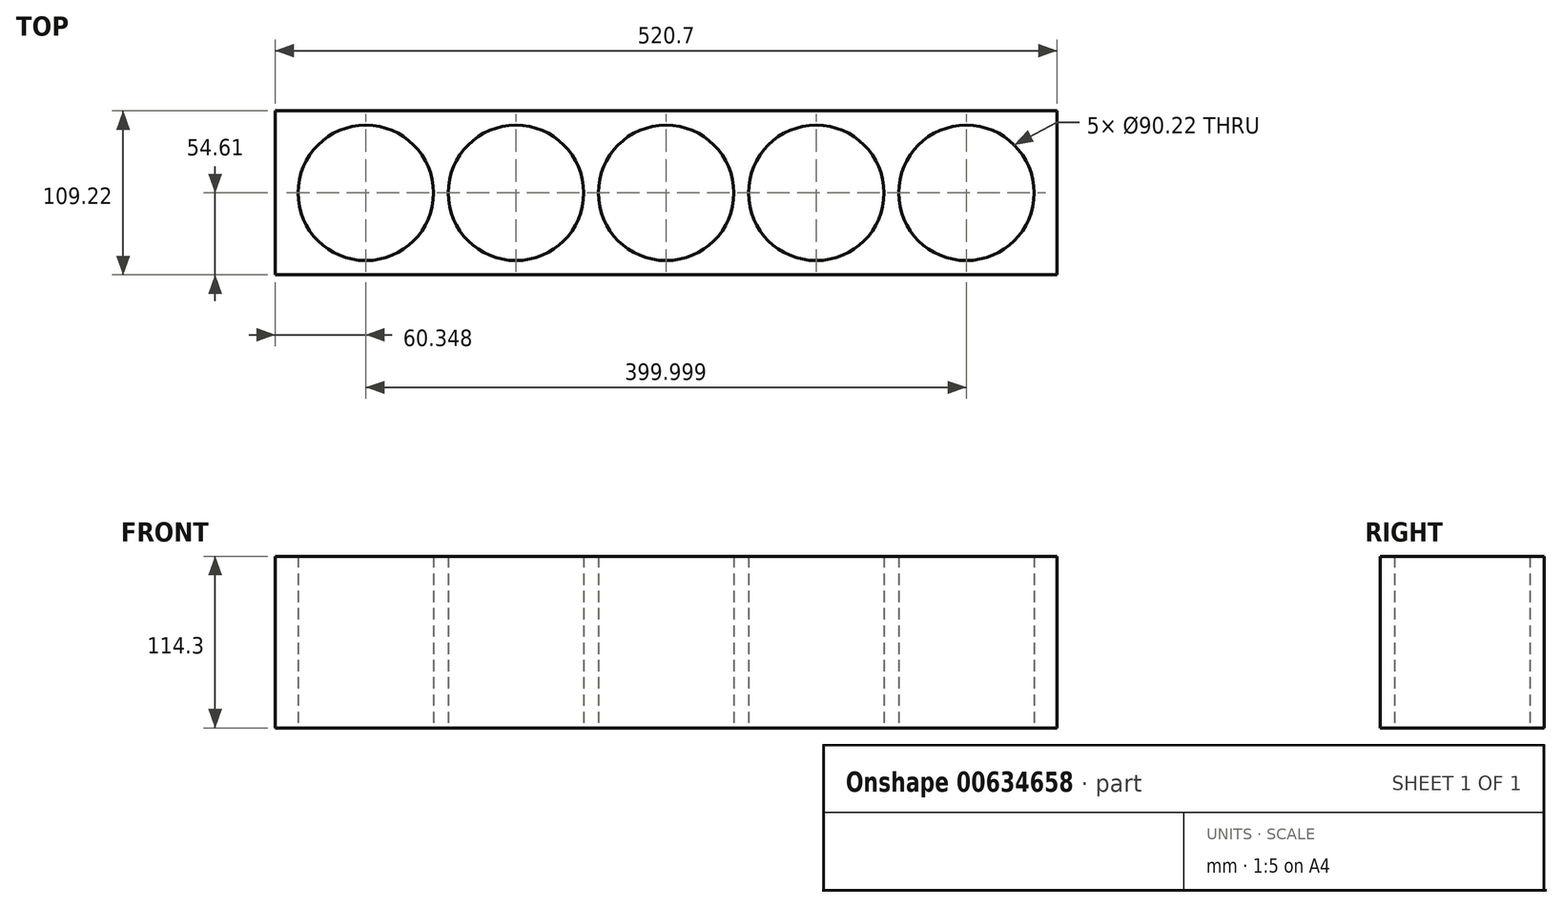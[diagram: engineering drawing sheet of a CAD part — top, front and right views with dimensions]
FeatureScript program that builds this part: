
annotation { "Feature Type Name" : "Feature", "Feature Type Description" : "" }
export const myFeature = defineFeature(function(context is Context, id is Id, definition is map)
    precondition{}
    {
        {
            var Q0;
            Q0=qCreatedBy(makeId("Top.planeOp"),FACE);
            var sketch = newSketch(context, id + "F0", { "sketchPlane" : qUnion([Q0])});
            skCircle(sketch, "E0", {"center": v(-175.23, 0) * mm, "radius": 45.11 * mm});
            skCircle(sketch, "E1.1.0.0", {"center": v(-75.23, 0) * mm, "radius": 45.11 * mm});
            skCircle(sketch, "E1.2.0.0", {"center": v(24.77, 0) * mm, "radius": 45.11 * mm});
            skCircle(sketch, "E1.3.0.0", {"center": v(124.77, 0) * mm, "radius": 45.11 * mm});
            skCircle(sketch, "E1.4.0.0", {"center": v(224.77, 0) * mm, "radius": 45.11 * mm});
            skLineSegment(sketch, "E1.direction1", {"start": v(-175.23, 0) * mm, "end": v(-75.23, 0) * mm, "construction": true});
            skLineSegment(sketch, "E2", {"start": v(-175.23, 0) * mm, "end": v(224.77, 0) * mm, "construction": true});
            skLineSegment(sketch, "E3.bottom", {"start": v(285.12, -54.6) * mm, "end": v(-235.58, -54.61) * mm});
            skLineSegment(sketch, "E3.top", {"start": v(285.12, 54.61) * mm, "end": v(-235.58, 54.6) * mm});
            skLineSegment(sketch, "E3.left", {"start": v(285.12, -54.6) * mm, "end": v(285.12, 54.61) * mm});
            skLineSegment(sketch, "E3.right", {"start": v(-235.58, -54.61) * mm, "end": v(-235.58, 54.6) * mm});
            skSolve(sketch);
        }
        {
            var Q0;
            Q0=makeQuery(id+"F0.imprint","IMPRINT",FACE,{"disambiguationData":[TD([[makeQuery(id+"F0.imprint","IMPRINT",EDGE,{"derivedFrom":sQuery(id+"F0.wireOp",EDGE,"E0")}),-1.0]])]});
            extrude(context, id + "F1", {"entities" : qUnion([Q0]), "depth" : 114.3 * mm, "offsetDistance" : 25.4 * mm});
        }
    });
